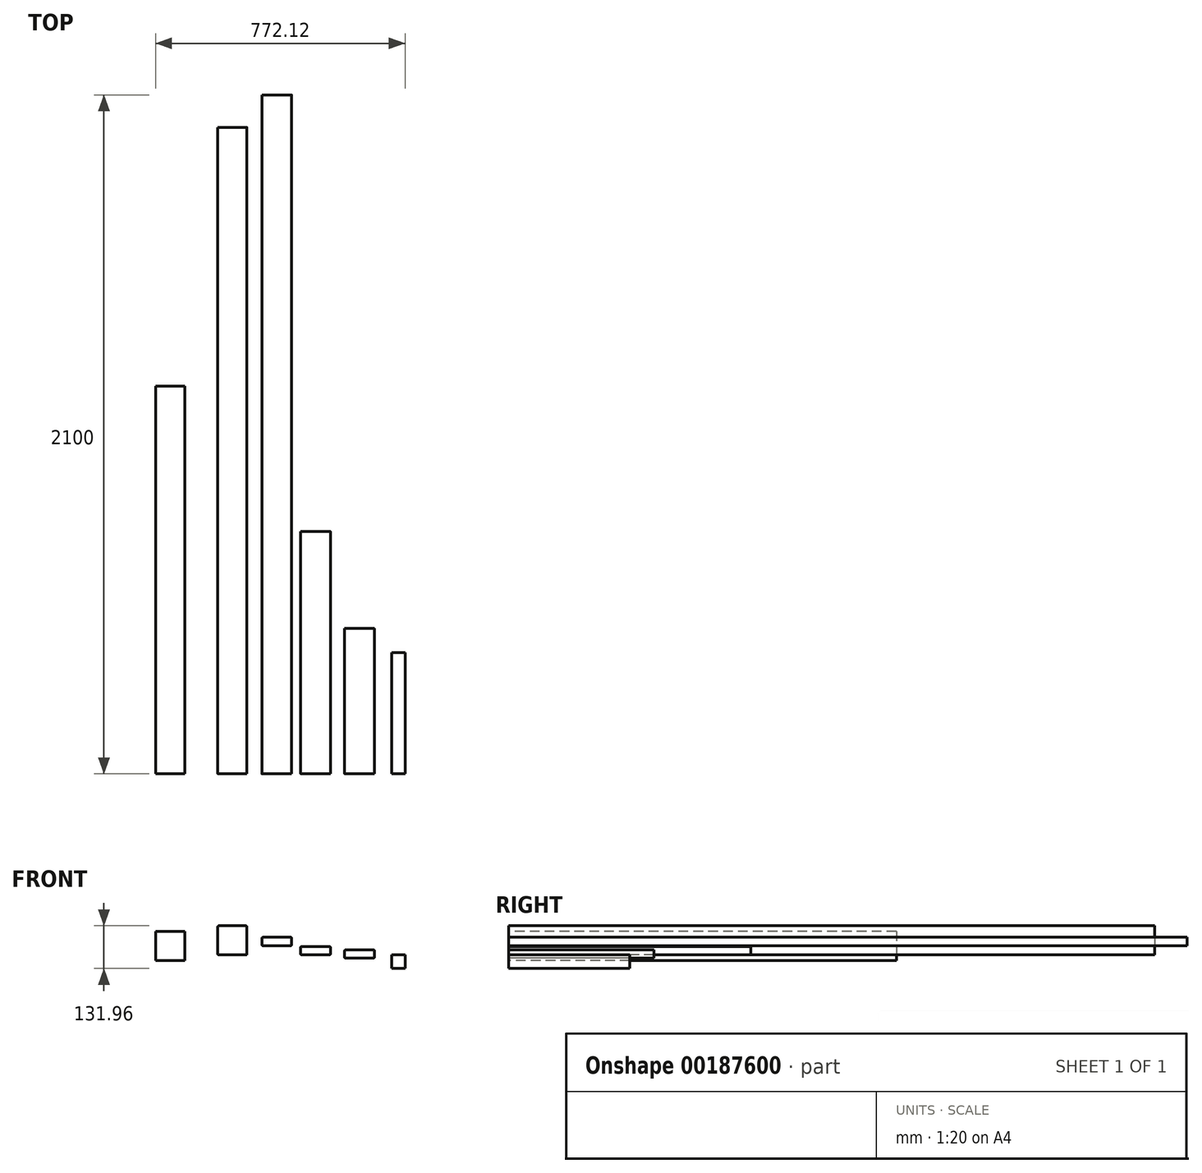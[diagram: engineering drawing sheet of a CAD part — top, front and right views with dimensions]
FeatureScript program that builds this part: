
annotation { "Feature Type Name" : "Feature", "Feature Type Description" : "" }
export const myFeature = defineFeature(function(context is Context, id is Id, definition is map)
    precondition{}
    {
        {
            var Q0;
            Q0=qCreatedBy(makeId("Front.planeOp"),FACE);
            var sketch = newSketch(context, id + "F0", { "sketchPlane" : qUnion([Q0])});
            skLineSegment(sketch, "E0.bottom", {"start": v(-75.42, 15.8) * mm, "end": v(16.58, 15.8) * mm});
            skLineSegment(sketch, "E0.top", {"start": v(-75.42, -10.2) * mm, "end": v(16.58, -10.2) * mm});
            skLineSegment(sketch, "E0.left", {"start": v(-75.42, 15.8) * mm, "end": v(-75.42, -10.2) * mm});
            skLineSegment(sketch, "E0.right", {"start": v(16.58, 15.8) * mm, "end": v(16.58, -10.2) * mm});
            skSolve(sketch);
        }
        {
            var Q0;
            Q0=makeQuery(id+"F0.imprint","IMPRINT",FACE,{"disambiguationData":[TD([[makeQuery(id+"F0.imprint","IMPRINT",EDGE,{"derivedFrom":sQuery(id+"F0.wireOp",EDGE,"E0.bottom")}),-1.0]])]});
            extrude(context, id + "F1", {"entities" : qUnion([Q0]), "oppositeDirection" : true, "depth" : 450 * mm});
        }
        {
            var Q0;
            Q0=makeQuery(id+"F1.opExtrude","SWEPT_EDGE",EDGE,{"disambiguationData":[OSD([sQuery(id+"F0.wireOp",EDGE,"E0.bottom"),sQuery(id+"F0.wireOp",EDGE,"E0.left")])]});
            var Q1;
            Q1=makeQuery(id+"F1.opExtrude","SWEPT_EDGE",EDGE,{"disambiguationData":[OSD([sQuery(id+"F0.wireOp",EDGE,"E0.top"),sQuery(id+"F0.wireOp",EDGE,"E0.left")])]});
            fillet(context, id + "F2", {"entities" : qUnion([Q0, Q1]), "radius" : 3 * mm, "tangentPropagation" : true, "allowEdgeOverflow" : false});
        }
        {
            var Q0;
            Q0=makeQuery(id+"F1.opExtrude","SWEPT_EDGE",EDGE,{"disambiguationData":[OSD([sQuery(id+"F0.wireOp",EDGE,"E0.bottom"),sQuery(id+"F0.wireOp",EDGE,"E0.right")])]});
            var Q1;
            Q1=makeQuery(id+"F1.opExtrude","SWEPT_EDGE",EDGE,{"disambiguationData":[OSD([sQuery(id+"F0.wireOp",EDGE,"E0.top"),sQuery(id+"F0.wireOp",EDGE,"E0.right")])]});
            fillet(context, id + "F3", {"entities" : qUnion([Q0, Q1]), "radius" : 3 * mm, "tangentPropagation" : true, "allowEdgeOverflow" : false});
        }
        {
            var Q0;
            Q0=qCreatedBy(makeId("Front.planeOp"),FACE);
            var sketch = newSketch(context, id + "F4", { "sketchPlane" : qUnion([Q0])});
            skLineSegment(sketch, "E1.bottom", {"start": v(-211.4, 26) * mm, "end": v(-119.4, 26) * mm});
            skLineSegment(sketch, "E1.top", {"start": v(-211.4, 0) * mm, "end": v(-119.4, 0) * mm});
            skLineSegment(sketch, "E1.left", {"start": v(-211.4, 26) * mm, "end": v(-211.4, 0) * mm});
            skLineSegment(sketch, "E1.right", {"start": v(-119.4, 26) * mm, "end": v(-119.4, 0) * mm});
            skSolve(sketch);
        }
        {
            var Q0;
            Q0=makeQuery(id+"F4.imprint","IMPRINT",FACE,{"disambiguationData":[TD([[makeQuery(id+"F4.imprint","IMPRINT",EDGE,{"derivedFrom":sQuery(id+"F4.wireOp",EDGE,"E1.bottom")}),-1.0]])]});
            extrude(context, id + "F5", {"entities" : qUnion([Q0]), "oppositeDirection" : true, "depth" : 750 * mm});
        }
        {
            var Q0;
            Q0=makeQuery(id+"F5.opExtrude","SWEPT_EDGE",EDGE,{"disambiguationData":[OSD([sQuery(id+"F4.wireOp",EDGE,"E1.bottom"),sQuery(id+"F4.wireOp",EDGE,"E1.left")])]});
            var Q1;
            Q1=makeQuery(id+"F5.opExtrude","SWEPT_EDGE",EDGE,{"disambiguationData":[OSD([sQuery(id+"F4.wireOp",EDGE,"E1.bottom"),sQuery(id+"F4.wireOp",EDGE,"E1.right")])]});
            var Q2;
            Q2=makeQuery(id+"F5.opExtrude","SWEPT_EDGE",EDGE,{"disambiguationData":[OSD([sQuery(id+"F4.wireOp",EDGE,"E1.top"),sQuery(id+"F4.wireOp",EDGE,"E1.right")])]});
            var Q3;
            Q3=makeQuery(id+"F5.opExtrude","SWEPT_EDGE",EDGE,{"disambiguationData":[OSD([sQuery(id+"F4.wireOp",EDGE,"E1.top"),sQuery(id+"F4.wireOp",EDGE,"E1.left")])]});
            fillet(context, id + "F6", {"entities" : qUnion([Q0, Q1, Q2, Q3]), "radius" : 3 * mm, "tangentPropagation" : true, "allowEdgeOverflow" : false});
        }
        {
            var Q0;
            Q0=qCreatedBy(makeId("Front.planeOp"),FACE);
            var sketch = newSketch(context, id + "F7", { "sketchPlane" : qUnion([Q0])});
            skLineSegment(sketch, "E2.bottom", {"start": v(-331.13, 54.54) * mm, "end": v(-239.13, 54.54) * mm});
            skLineSegment(sketch, "E2.top", {"start": v(-331.13, 28.54) * mm, "end": v(-239.13, 28.54) * mm});
            skLineSegment(sketch, "E2.left", {"start": v(-331.13, 54.54) * mm, "end": v(-331.13, 28.54) * mm});
            skLineSegment(sketch, "E2.right", {"start": v(-239.13, 54.54) * mm, "end": v(-239.13, 28.54) * mm});
            skSolve(sketch);
        }
        {
            var Q0;
            Q0=makeQuery(id+"F7.imprint","IMPRINT",FACE,{"disambiguationData":[TD([[makeQuery(id+"F7.imprint","IMPRINT",EDGE,{"derivedFrom":sQuery(id+"F7.wireOp",EDGE,"E2.bottom")}),-1.0]])]});
            extrude(context, id + "F8", {"entities" : qUnion([Q0]), "oppositeDirection" : true, "depth" : 2100 * mm});
        }
        {
            var Q0;
            Q0=makeQuery(id+"F8.opExtrude","SWEPT_EDGE",EDGE,{"disambiguationData":[OSD([sQuery(id+"F7.wireOp",EDGE,"E2.bottom"),sQuery(id+"F7.wireOp",EDGE,"E2.left")])]});
            var Q1;
            Q1=makeQuery(id+"F8.opExtrude","SWEPT_EDGE",EDGE,{"disambiguationData":[OSD([sQuery(id+"F7.wireOp",EDGE,"E2.bottom"),sQuery(id+"F7.wireOp",EDGE,"E2.right")])]});
            var Q2;
            Q2=makeQuery(id+"F8.opExtrude","SWEPT_EDGE",EDGE,{"disambiguationData":[OSD([sQuery(id+"F7.wireOp",EDGE,"E2.top"),sQuery(id+"F7.wireOp",EDGE,"E2.right")])]});
            var Q3;
            Q3=makeQuery(id+"F8.opExtrude","SWEPT_EDGE",EDGE,{"disambiguationData":[OSD([sQuery(id+"F7.wireOp",EDGE,"E2.top"),sQuery(id+"F7.wireOp",EDGE,"E2.left")])]});
            fillet(context, id + "F9", {"entities" : qUnion([Q0, Q1, Q2, Q3]), "radius" : 3 * mm, "tangentPropagation" : true, "allowEdgeOverflow" : false});
        }
        {
            var Q0;
            Q0=qCreatedBy(makeId("Front.planeOp"),FACE);
            var sketch = newSketch(context, id + "F10", { "sketchPlane" : qUnion([Q0])});
            skLineSegment(sketch, "E3.bottom", {"start": v(69.72, 0.04) * mm, "end": v(111.72, 0.04) * mm});
            skLineSegment(sketch, "E3.top", {"start": v(69.72, -41.96) * mm, "end": v(111.72, -41.96) * mm});
            skLineSegment(sketch, "E3.left", {"start": v(69.72, 0.04) * mm, "end": v(69.72, -41.96) * mm});
            skLineSegment(sketch, "E3.right", {"start": v(111.72, 0.04) * mm, "end": v(111.72, -41.96) * mm});
            skSolve(sketch);
        }
        {
            var Q0;
            Q0=makeQuery(id+"F10.imprint","IMPRINT",FACE,{"disambiguationData":[TD([[makeQuery(id+"F10.imprint","IMPRINT",EDGE,{"derivedFrom":sQuery(id+"F10.wireOp",EDGE,"E3.bottom")}),-1.0]])]});
            extrude(context, id + "F11", {"entities" : qUnion([Q0]), "oppositeDirection" : true, "depth" : 375 * mm});
        }
        {
            var Q0;
            Q0=qCreatedBy(makeId("Front.planeOp"),FACE);
            var sketch = newSketch(context, id + "F12", { "sketchPlane" : qUnion([Q0])});
            skLineSegment(sketch, "E4.bottom", {"start": v(-467.83, 90) * mm, "end": v(-377.83, 90) * mm});
            skLineSegment(sketch, "E4.top", {"start": v(-467.83, 0) * mm, "end": v(-377.83, 0) * mm});
            skLineSegment(sketch, "E4.left", {"start": v(-467.83, 90) * mm, "end": v(-467.83, 0) * mm});
            skLineSegment(sketch, "E4.right", {"start": v(-377.83, 90) * mm, "end": v(-377.83, 0) * mm});
            skSolve(sketch);
        }
        {
            var Q0;
            Q0=makeQuery(id+"F12.imprint","IMPRINT",FACE,{"disambiguationData":[TD([[makeQuery(id+"F12.imprint","IMPRINT",EDGE,{"derivedFrom":sQuery(id+"F12.wireOp",EDGE,"E4.bottom")}),-1.0]])]});
            extrude(context, id + "F13", {"entities" : qUnion([Q0]), "oppositeDirection" : true, "depth" : 2000 * mm});
        }
        {
            var Q0;
            Q0=makeQuery(id+"F13.opExtrude","SWEPT_EDGE",EDGE,{"disambiguationData":[OSD([sQuery(id+"F12.wireOp",EDGE,"E4.bottom"),sQuery(id+"F12.wireOp",EDGE,"E4.left")])]});
            var Q1;
            Q1=makeQuery(id+"F13.opExtrude","SWEPT_EDGE",EDGE,{"disambiguationData":[OSD([sQuery(id+"F12.wireOp",EDGE,"E4.bottom"),sQuery(id+"F12.wireOp",EDGE,"E4.right")])]});
            var Q2;
            Q2=makeQuery(id+"F13.opExtrude","SWEPT_EDGE",EDGE,{"disambiguationData":[OSD([sQuery(id+"F12.wireOp",EDGE,"E4.top"),sQuery(id+"F12.wireOp",EDGE,"E4.left")])]});
            var Q3;
            Q3=makeQuery(id+"F13.opExtrude","SWEPT_EDGE",EDGE,{"disambiguationData":[OSD([sQuery(id+"F12.wireOp",EDGE,"E4.top"),sQuery(id+"F12.wireOp",EDGE,"E4.right")])]});
            fillet(context, id + "F14", {"entities" : qUnion([Q0, Q1, Q2, Q3]), "radius" : 3 * mm, "tangentPropagation" : true, "allowEdgeOverflow" : false});
        }
        {
            var Q0;
            Q0=qCreatedBy(makeId("Front.planeOp"),FACE);
            var sketch = newSketch(context, id + "F15", { "sketchPlane" : qUnion([Q0])});
            skLineSegment(sketch, "E5.bottom", {"start": v(-660.4, 73.23) * mm, "end": v(-570.4, 73.23) * mm});
            skLineSegment(sketch, "E5.top", {"start": v(-660.4, -16.77) * mm, "end": v(-570.4, -16.77) * mm});
            skLineSegment(sketch, "E5.left", {"start": v(-660.4, 73.23) * mm, "end": v(-660.4, -16.77) * mm});
            skLineSegment(sketch, "E5.right", {"start": v(-570.4, 73.23) * mm, "end": v(-570.4, -16.77) * mm});
            skSolve(sketch);
        }
        {
            var Q0;
            Q0=makeQuery(id+"F15.imprint","IMPRINT",FACE,{"disambiguationData":[TD([[makeQuery(id+"F15.imprint","IMPRINT",EDGE,{"derivedFrom":sQuery(id+"F15.wireOp",EDGE,"E5.bottom")}),-1.0]])]});
            extrude(context, id + "F16", {"entities" : qUnion([Q0]), "oppositeDirection" : true, "depth" : 1200 * mm});
        }
    });
